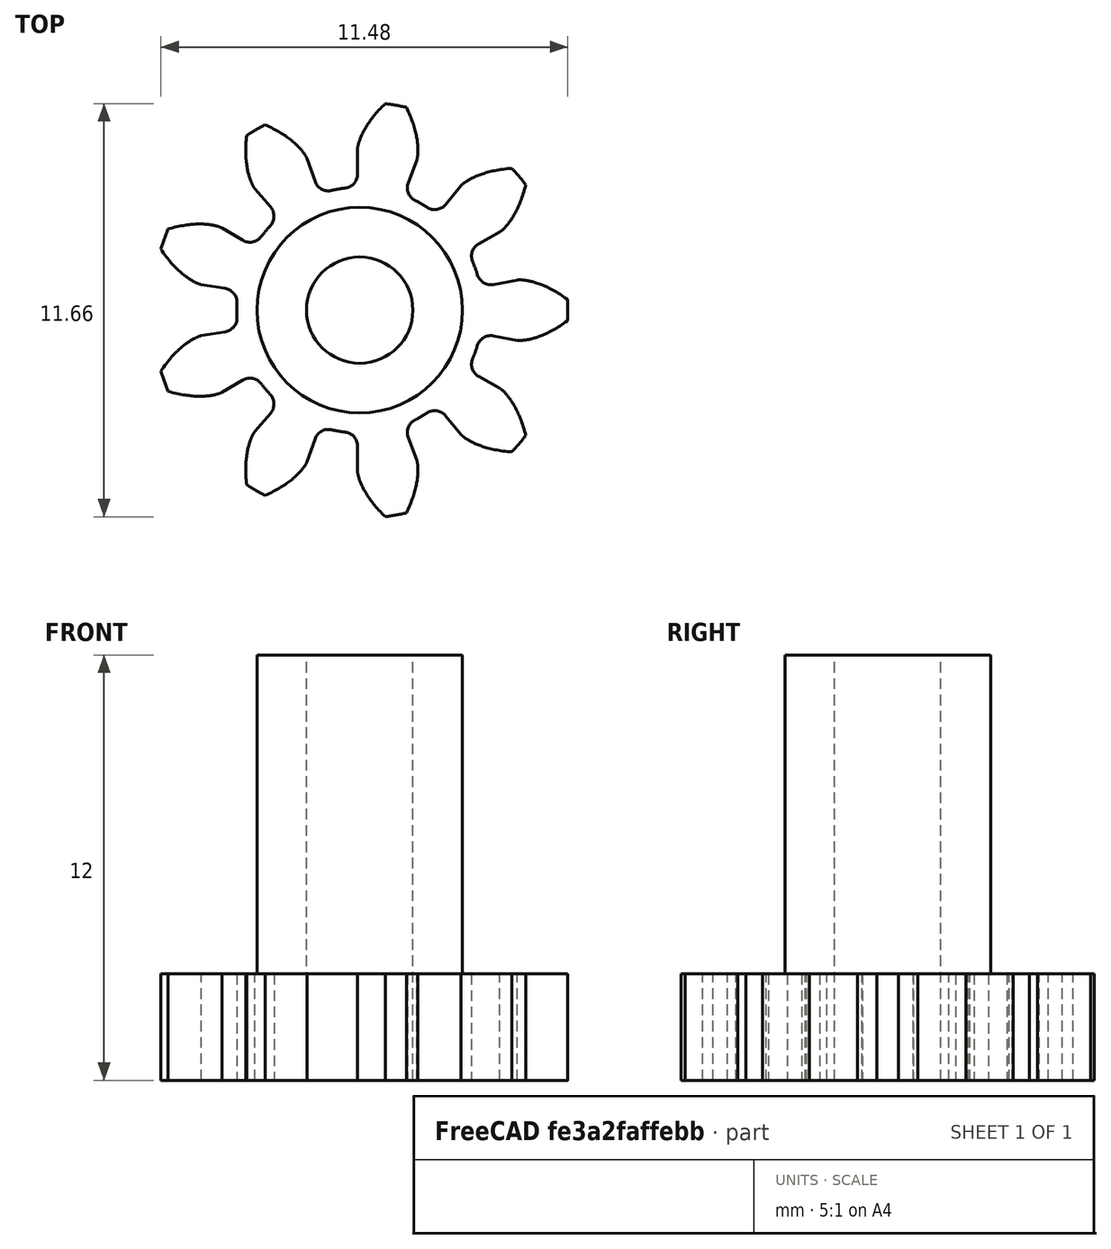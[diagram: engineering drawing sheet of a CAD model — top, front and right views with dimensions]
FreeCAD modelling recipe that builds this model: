
FCSTD DOCUMENT  (FreeCAD 0.17R13541 (Git))
Label: gear 9 exterior shaft (new)
License: All rights reserved
LicenseURL: http://en.wikipedia.org/wiki/All_rights_reserved
objects: Part::Cylinder×3, Part::Cut×2, Part::Part2DObjectPython×1, Part::Extrusion×1, Part::MultiFuse×1
note: 8 computed .brp shape members not serialized (recipe doc carries the construction recipe); baked Part::Feature solids carry a one-line shape summary decoded from their .brp

FEATURE [Part::Part2DObjectPython] InvoluteGear  label="Engranaje 3 raw"  # Draft 2D object (typed FeaturePython)
  ExternalGear = true
  HighPrecision = true
  Modules = 1.067
  NumberOfTeeth = 9
  PressureAngle = 20
  expr: Modules = 1.0669999999999999
FEATURE [Part::Extrusion] Extrude  label="Engranaje 3 extruido"
  Base = -> InvoluteGear
  Dir = (0,0,1)
  DirMode = 2
  FaceMakerClass = Part::FaceMakerBullseye
  LengthFwd = 3
  LengthRev = 0
  Solid = true
  Symmetric = false
FEATURE [Part::Cylinder] Cylinder  label="Cilindro"
  Angle = 360
  AttacherType = Attacher::AttachEngine3D
  Height = 10
  Radius = 1.5
FEATURE [Part::Cut] Cut  label="Engranaje 3 agujereado"
  Base = -> Extrude
  Refine = true
  Tool = -> Cylinder
FEATURE [Part::Cylinder] Cylinder001  label="Cilindro exterior"
  Angle = 360
  AttacherType = Attacher::AttachEngine3D
  Height = 9
  Placement = pos=(0,0,3) rot=(0,0,1;0rad)
  Radius = 2.9
FEATURE [Part::Cylinder] Cylinder002  label="Cilindro interior"
  Angle = 360
  AttacherType = Attacher::AttachEngine3D
  Height = 21
  Placement = pos=(0,0,-2) rot=(0,0,1;0rad)
  Radius = 1.5
FEATURE [Part::MultiFuse] Fusion
  Refine = true
  Shapes = -> [Cut,Cylinder001]
FEATURE [Part::Cut] Cut001  label="Engranaje 3 final"
  Base = -> Fusion
  Refine = true
  Tool = -> Cylinder002
